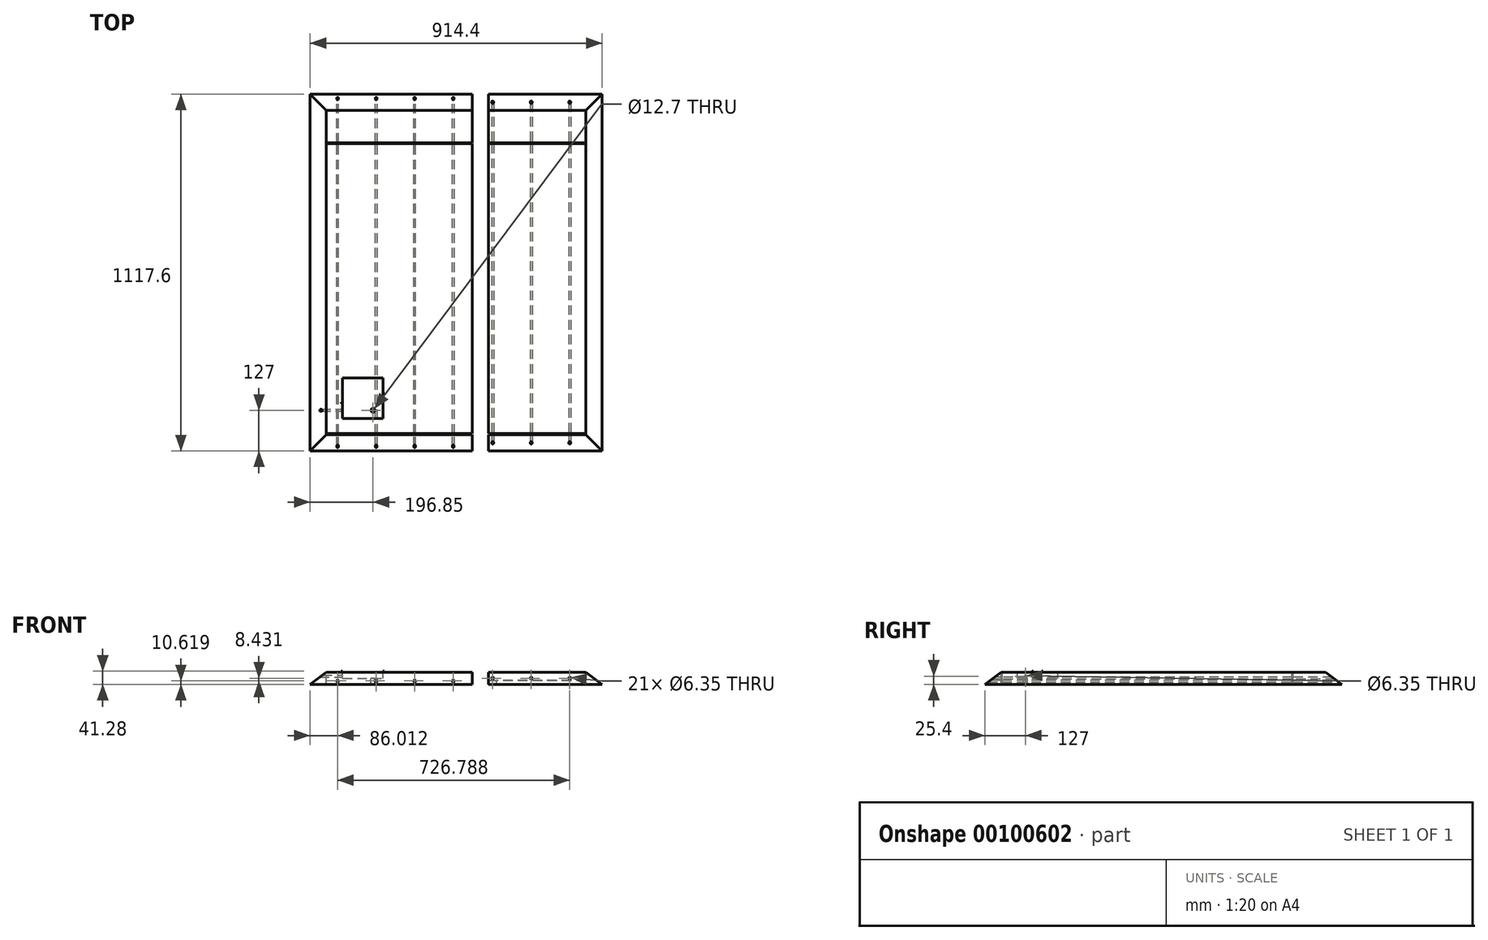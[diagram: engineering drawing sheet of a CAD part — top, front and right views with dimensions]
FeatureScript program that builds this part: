
annotation { "Feature Type Name" : "Feature", "Feature Type Description" : "" }
export const myFeature = defineFeature(function(context is Context, id is Id, definition is map)
    precondition{}
    {
        {
            var Q0;
            Q0=qCreatedBy(makeId("Top.planeOp"),FACE);
            var sketch = newSketch(context, id + "F0", { "sketchPlane" : qUnion([Q0])});
            skLineSegment(sketch, "E0.bottom", {"start": v(-406.4, 558.8) * mm, "end": v(50.8, 558.8) * mm});
            skLineSegment(sketch, "E0.top", {"start": v(-406.4, -558.8) * mm, "end": v(50.8, -558.8) * mm});
            skLineSegment(sketch, "E0.left", {"start": v(-406.4, 558.8) * mm, "end": v(-406.4, -558.8) * mm});
            skLineSegment(sketch, "E0.right", {"start": v(406.4, 558.8) * mm, "end": v(406.4, -558.8) * mm});
            skPoint(sketch, "E1", {"position": v(0, 558.8) * mm});
            skPoint(sketch, "E2.positionSnap0", {"position": v(406.4, 0) * mm});
            skLineSegment(sketch, "E3", {"start": v(101.6, 558.8) * mm, "end": v(101.6, -558.8) * mm});
            skLineSegment(sketch, "E4", {"start": v(50.8, 558.8) * mm, "end": v(50.8, -558.8) * mm});
            skLineSegment(sketch, "E5.trimOffspring", {"start": v(101.6, 558.8) * mm, "end": v(406.4, 558.8) * mm});
            skLineSegment(sketch, "E6.trimOffspring", {"start": v(101.6, -558.8) * mm, "end": v(406.4, -558.8) * mm});
            skSolve(sketch);
        }
        {
            var Q0;
            Q0=makeQuery(id+"F0.imprint","IMPRINT",FACE,{"disambiguationData":[TD([[makeQuery(id+"F0.imprint","IMPRINT",EDGE,{"derivedFrom":sQuery(id+"F0.wireOp",EDGE,"E0.bottom")}),-1.0]])]});
            extrude(context, id + "F1", {"entities" : qUnion([Q0]), "depth" : 38.1 * mm});
        }
        {
            var Q0;
            Q0=makeQuery(id+"F1.opExtrude","CAP_EDGE",EDGE,{"disambiguationData":[OSD([sQuery(id+"F0.wireOp",EDGE,"E0.top")])],"isStart":false});
            var Q1;
            Q1=makeQuery(id+"F1.opExtrude","CAP_EDGE",EDGE,{"disambiguationData":[OSD([sQuery(id+"F0.wireOp",EDGE,"E0.left")])],"isStart":false});
            var Q2;
            Q2=makeQuery(id+"F1.opExtrude","CAP_EDGE",EDGE,{"disambiguationData":[OSD([sQuery(id+"F0.wireOp",EDGE,"E0.bottom")])],"isStart":false});
            chamfer(context, id + "F2", {"entities" : qUnion([Q0, Q1, Q2]), "width" : 38.1 * mm, "tangentPropagation" : true});
        }
        {
            var Q0;
            Q0=qCreatedBy(makeId("Front.planeOp"),FACE);
            var sketch = newSketch(context, id + "F3", { "sketchPlane" : qUnion([Q0])});
            skLineSegment(sketch, "E7.bottom", {"start": v(139.7, 0) * mm, "end": v(88.9, 0) * mm});
            skLineSegment(sketch, "E7.top", {"start": v(139.7, 50.8) * mm, "end": v(88.9, 50.8) * mm});
            skLineSegment(sketch, "E7.left", {"start": v(139.7, 0) * mm, "end": v(139.7, 50.8) * mm});
            skLineSegment(sketch, "E7.right", {"start": v(88.9, 0) * mm, "end": v(88.9, 50.8) * mm});
            skPoint(sketch, "E8", {"position": v(114.3, 0) * mm});
            skSolve(sketch);
        }
        {
            var Q0;
            Q0=makeQuery(id+"F3.imprint","IMPRINT",FACE,{"disambiguationData":[TD([[makeQuery(id+"F3.imprint","IMPRINT",EDGE,{"derivedFrom":sQuery(id+"F3.wireOp",EDGE,"E7.bottom")}),-1.0]])]});
            extrude(context, id + "F4", {"entities" : qUnion([Q0]), "operationType" : NewBodyOperationType.REMOVE, "oppositeDirection" : true, "depth" : 406.4 * mm, "hasSecondDirection" : true, "secondDirectionOppositeDirection" : false, "secondDirectionDepth" : 406.4 * mm});
        }
        {
            var Q0;
            Q0=makeQuery(id+"F1.opExtrude","CAP_FACE",FACE,{"disambiguationData":[OSD([sQuery(id+"F0.wireOp",EDGE,"E0.bottom"),sQuery(id+"F0.wireOp",EDGE,"E0.top"),sQuery(id+"F0.wireOp",EDGE,"E0.left"),sQuery(id+"F0.wireOp",EDGE,"E0.right")])],"isStart":false});
            var sketch = newSketch(context, id + "F5", { "sketchPlane" : qUnion([Q0])});
            skLineSegment(sketch, "E9.bottom", {"start": v(-165.1, -520.7) * mm, "end": v(-368.3, -520.7) * mm});
            skLineSegment(sketch, "E9.top", {"start": v(-165.1, -368.3) * mm, "end": v(-368.3, -368.3) * mm});
            skLineSegment(sketch, "E9.left", {"start": v(-165.1, -520.7) * mm, "end": v(-165.1, -368.3) * mm});
            skLineSegment(sketch, "E9.right", {"start": v(-368.3, -520.7) * mm, "end": v(-368.3, -368.3) * mm});
            skSolve(sketch);
        }
        {
            var Q0;
            Q0=makeQuery(id+"F5.imprint","IMPRINT",FACE,{"disambiguationData":[TD([[makeQuery(id+"F5.imprint","IMPRINT",EDGE,{"derivedFrom":sQuery(id+"F5.wireOp",EDGE,"E9.bottom")}),-1.0]])]});
            var Q1;
            Q1=makeQuery(id+"F5.imprint","IMPRINT",FACE,{"disambiguationData":[TD([[makeQuery(id+"F5.imprint","IMPRINT",EDGE,{"derivedFrom":sQuery(id+"F5.wireOp",EDGE,"E9.bottom")}),1.0]])]});
            extrude(context, id + "F6", {"entities" : qUnion([Q0, Q1]), "operationType" : NewBodyOperationType.REMOVE, "oppositeDirection" : true, "depth" : 25.4 * mm});
        }
        {
            var Q0;
            Q0=makeQuery(id+"F1.opExtrude","SWEPT_BODY",BODY,{"disambiguationData":[OSD([sQuery(id+"F0.wireOp",EDGE,"E0.bottom"),sQuery(id+"F0.wireOp",EDGE,"E0.top"),sQuery(id+"F0.wireOp",EDGE,"E0.left"),sQuery(id+"F0.wireOp",EDGE,"E0.right")])]});
            deleteBodies(context, id + "F7", {"entities" : qUnion([Q0])});
        }
        {
            var Q0;
            Q0 = qSketchRegion(id + "F0", true);
            extrude(context, id + "F8", {"entities" : qUnion([Q0]), "depth" : 38.1 * mm});
        }
        {
            var Q0;
            Q0=makeQuery(id+"F8.opExtrude","SWEPT_FACE",FACE,{"disambiguationData":[OSD([sQuery(id+"F0.wireOp",EDGE,"E6.trimOffspring")])]});
            var sketch = newSketch(context, id + "F9", { "sketchPlane" : qUnion([Q0])});
            skLineSegment(sketch, "E10", {"start": v(406.4, 38.1) * mm, "end": v(457.2, 0) * mm});
            skLineSegment(sketch, "E11", {"start": v(457.2, 0) * mm, "end": v(406.4, 0) * mm});
            skLineSegment(sketch, "E12", {"start": v(406.4, 0) * mm, "end": v(101.6, 0) * mm});
            skLineSegment(sketch, "E13", {"start": v(101.6, 0) * mm, "end": v(101.6, 38.1) * mm});
            skLineSegment(sketch, "E14", {"start": v(101.6, 38.1) * mm, "end": v(406.4, 38.1) * mm});
            skSolve(sketch);
        }
        {
            var Q0;
            Q0=makeQuery(id+"F9.imprint","IMPRINT",FACE,{"disambiguationData":[TD([[makeQuery(id+"F9.imprint","IMPRINT",EDGE,{"derivedFrom":sQuery(id+"F9.wireOp",EDGE,"E10")}),-1.0]])]});
            var Q1;
            Q1=makeQuery(id+"F8.opExtrude","SWEPT_FACE",FACE,{"disambiguationData":[OSD([sQuery(id+"F0.wireOp",EDGE,"E5.trimOffspring")])]});
            extrude(context, id + "F10", {"entities" : qUnion([Q0]), "operationType" : NewBodyOperationType.ADD, "endBound" : BoundingType.UP_TO_SURFACE, "oppositeDirection" : true, "endBoundEntityFace" : qUnion([Q1]), "depth" : 25.4 * mm});
        }
        {
            var Q0;
            Q0 = qSketchRegion(id + "F9", true);
            var Q1;
            Q1=makeQuery(id+"F8.opExtrude","SWEPT_FACE",FACE,{"disambiguationData":[OSD([sQuery(id+"F0.wireOp",EDGE,"E5.trimOffspring")])]});
            extrude(context, id + "F11", {"entities" : qUnion([Q0]), "operationType" : NewBodyOperationType.ADD, "endBound" : BoundingType.UP_TO_SURFACE, "oppositeDirection" : true, "endBoundEntityFace" : qUnion([Q1]), "depth" : 25.4 * mm});
        }
        {
            var Q0;
            Q0=makeQuery(id+"F8.opExtrude","SWEPT_FACE",FACE,{"disambiguationData":[OSD([sQuery(id+"F0.wireOp",EDGE,"E0.top")])]});
            var sketch = newSketch(context, id + "F12", { "sketchPlane" : qUnion([Q0])});
            skLineSegment(sketch, "E15", {"start": v(-406.4, 38.1) * mm, "end": v(-457.2, 0) * mm});
            skLineSegment(sketch, "E16", {"start": v(-457.2, 0) * mm, "end": v(-406.4, 0) * mm});
            skLineSegment(sketch, "E17", {"start": v(-406.4, 0) * mm, "end": v(50.8, 0) * mm});
            skLineSegment(sketch, "E18", {"start": v(50.8, 0) * mm, "end": v(50.8, 38.1) * mm});
            skLineSegment(sketch, "E19", {"start": v(50.8, 38.1) * mm, "end": v(-406.4, 38.1) * mm});
            skSolve(sketch);
        }
        {
            var Q0;
            Q0 = qSketchRegion(id + "F12", true);
            var Q1;
            Q1=makeQuery(id+"F8.opExtrude","SWEPT_FACE",FACE,{"disambiguationData":[OSD([sQuery(id+"F0.wireOp",EDGE,"E0.bottom")])]});
            extrude(context, id + "F13", {"entities" : qUnion([Q0]), "operationType" : NewBodyOperationType.ADD, "endBound" : BoundingType.UP_TO_SURFACE, "oppositeDirection" : true, "endBoundEntityFace" : qUnion([Q1]), "depth" : 25.4 * mm});
        }
        {
            var Q0;
            Q0=makeQuery(id+"F8.opExtrude","CAP_FACE",FACE,{"disambiguationData":[OSD([sQuery(id+"F0.wireOp",EDGE,"E0.bottom"),sQuery(id+"F0.wireOp",EDGE,"E0.top"),sQuery(id+"F0.wireOp",EDGE,"E0.left"),sQuery(id+"F0.wireOp",EDGE,"E4")])],"isStart":false});
            var sketch = newSketch(context, id + "F14", { "sketchPlane" : qUnion([Q0])});
            skLineSegment(sketch, "E20.bottom", {"start": v(-355.6, -457.2) * mm, "end": v(-228.6, -457.2) * mm});
            skLineSegment(sketch, "E20.top", {"start": v(-355.6, -330.2) * mm, "end": v(-228.6, -330.2) * mm});
            skLineSegment(sketch, "E20.left", {"start": v(-355.6, -457.2) * mm, "end": v(-355.6, -330.2) * mm});
            skLineSegment(sketch, "E20.right", {"start": v(-228.6, -457.2) * mm, "end": v(-228.6, -330.2) * mm});
            skSolve(sketch);
        }
        {
            var Q0;
            Q0=makeQuery(id+"F14.imprint","IMPRINT",FACE,{"disambiguationData":[TD([[makeQuery(id+"F14.imprint","IMPRINT",EDGE,{"derivedFrom":sQuery(id+"F14.wireOp",EDGE,"E20.bottom")}),1.0]])]});
            extrude(context, id + "F15", {"entities" : qUnion([Q0]), "operationType" : NewBodyOperationType.REMOVE, "oppositeDirection" : true, "depth" : 19.05 * mm});
        }
        {
            var Q0;
            Q0=makeQuery(id+"F15.boolean.opBoolean","COPY",FACE,{"derivedFrom":makeQuery(id+"F15.opExtrude","CAP_FACE",FACE,{"disambiguationData":[OSD([sQuery(id+"F14.wireOp",EDGE,"E20.bottom"),sQuery(id+"F14.wireOp",EDGE,"E20.top"),sQuery(id+"F14.wireOp",EDGE,"E20.left"),sQuery(id+"F14.wireOp",EDGE,"E20.right")])],"isStart":false})});
            var sketch = newSketch(context, id + "F16", { "sketchPlane" : qUnion([Q0])});
            skCircle(sketch, "E21", {"center": v(-260.35, -431.8) * mm, "radius": 6.35 * mm});
            skSolve(sketch);
        }
        {
            var Q0;
            Q0 = qSketchRegion(id + "F16", true);
            extrude(context, id + "F17", {"entities" : qUnion([Q0]), "operationType" : NewBodyOperationType.REMOVE, "oppositeDirection" : true, "depth" : 25.4 * mm});
        }
        {
            var Q0;
            Q0=makeQuery(id+"F15.boolean.opBoolean","COPY",FACE,{"derivedFrom":makeQuery(id+"F15.opExtrude","SWEPT_FACE",FACE,{"disambiguationData":[OSD([sQuery(id+"F14.wireOp",EDGE,"E20.left")])]})});
            var sketch = newSketch(context, id + "F18", { "sketchPlane" : qUnion([Q0])});
            skCircle(sketch, "E22", {"center": v(-431.8, 25.4) * mm, "radius": 3.18 * mm});
            skSolve(sketch);
        }
        {
            var Q0;
            Q0=makeQuery(id+"F18.imprint","IMPRINT",FACE,{"disambiguationData":[TD([[makeQuery(id+"F18.imprint","IMPRINT",EDGE,{"derivedFrom":sQuery(id+"F18.wireOp",EDGE,"E22")}),1.0]])]});
            extrude(context, id + "F19", {"entities" : qUnion([Q0]), "operationType" : NewBodyOperationType.REMOVE, "endBound" : BoundingType.THROUGH_ALL, "oppositeDirection" : true, "depth" : 25.4 * mm});
        }
        {
            var Q0;
            Q0=makeQuery(id+"F8.opExtrude","CAP_FACE",FACE,{"disambiguationData":[OSD([sQuery(id+"F0.wireOp",EDGE,"E0.bottom"),sQuery(id+"F0.wireOp",EDGE,"E0.top"),sQuery(id+"F0.wireOp",EDGE,"E0.left"),sQuery(id+"F0.wireOp",EDGE,"E4")])],"isStart":false});
            var sketch = newSketch(context, id + "F20", { "sketchPlane" : qUnion([Q0])});
            skLineSegment(sketch, "E23.bottom", {"start": v(-361.95, -463.55) * mm, "end": v(-222.25, -463.55) * mm});
            skLineSegment(sketch, "E23.top", {"start": v(-361.95, -323.85) * mm, "end": v(-222.25, -323.85) * mm});
            skLineSegment(sketch, "E23.left", {"start": v(-361.95, -463.55) * mm, "end": v(-361.95, -323.85) * mm});
            skLineSegment(sketch, "E23.right", {"start": v(-222.25, -463.55) * mm, "end": v(-222.25, -323.85) * mm});
            skSolve(sketch);
        }
        {
            var Q0;
            Q0=makeQuery(id+"F20.imprint","IMPRINT",FACE,{"disambiguationData":[TD([[makeQuery(id+"F20.imprint","IMPRINT",EDGE,{"derivedFrom":makeQuery(id+"F15.boolean.opBoolean","COPY",EDGE,{"derivedFrom":makeQuery(id+"F15.opExtrude","CAP_EDGE",EDGE,{"disambiguationData":[OSD([sQuery(id+"F14.wireOp",EDGE,"E20.bottom")])],"isStart":true})})}),1.0]])]});
            var Q1;
            Q1=makeQuery(id+"F20.imprint","IMPRINT",FACE,{"disambiguationData":[TD([[makeQuery(id+"F20.imprint","IMPRINT",EDGE,{"derivedFrom":sQuery(id+"F20.wireOp",EDGE,"E23.bottom")}),1.0]])]});
            extrude(context, id + "F21", {"entities" : qUnion([Q0, Q1]), "depth" : 3.17 * mm});
        }
        {
            var Q0;
            Q0=makeQuery(id+"F21.opExtrude","CAP_FACE",FACE,{"disambiguationData":[OSD([sQuery(id+"F20.wireOp",EDGE,"E23.bottom"),sQuery(id+"F20.wireOp",EDGE,"E23.top"),sQuery(id+"F20.wireOp",EDGE,"E23.left"),sQuery(id+"F20.wireOp",EDGE,"E23.right")])],"isStart":false});
            var sketch = newSketch(context, id + "F22", { "sketchPlane" : qUnion([Q0])});
            skCircle(sketch, "E24", {"center": v(-357.51, -378.81) * mm, "radius": 1.65 * mm});
            skLineSegment(sketch, "E25", {"start": v(-361.95, -393.7) * mm, "end": v(-222.25, -393.7) * mm, "construction": true});
            skLineSegment(sketch, "E26", {"start": v(-292.1, -323.85) * mm, "end": v(-292.1, -463.55) * mm, "construction": true});
            skLineSegment(sketch, "E27.MirrorCS", {"start": v(-222.25, -393.7) * mm, "end": v(-361.95, -393.7) * mm, "construction": true});
            skCircle(sketch, "E28.MirrorC", {"center": v(-226.69, -378.81) * mm, "radius": 1.65 * mm});
            skCircle(sketch, "E29.MirrorC", {"center": v(-226.69, -408.59) * mm, "radius": 1.65 * mm});
            skCircle(sketch, "E30.MirrorC", {"center": v(-357.51, -408.59) * mm, "radius": 1.65 * mm});
            skSolve(sketch);
        }
        {
            var Q0;
            Q0=makeQuery(id+"F22.imprint","IMPRINT",FACE,{"disambiguationData":[TD([[makeQuery(id+"F22.imprint","IMPRINT",EDGE,{"derivedFrom":sQuery(id+"F22.wireOp",EDGE,"E30.MirrorC")}),-1.0]])]});
            var Q1;
            Q1=makeQuery(id+"F22.imprint","IMPRINT",FACE,{"disambiguationData":[TD([[makeQuery(id+"F22.imprint","IMPRINT",EDGE,{"derivedFrom":sQuery(id+"F22.wireOp",EDGE,"E29.MirrorC")}),1.0]])]});
            var Q2;
            Q2=makeQuery(id+"F22.imprint","IMPRINT",FACE,{"disambiguationData":[TD([[makeQuery(id+"F22.imprint","IMPRINT",EDGE,{"derivedFrom":sQuery(id+"F22.wireOp",EDGE,"E28.MirrorC")}),-1.0]])]});
            var Q3;
            Q3=makeQuery(id+"F22.imprint","IMPRINT",FACE,{"disambiguationData":[TD([[makeQuery(id+"F22.imprint","IMPRINT",EDGE,{"derivedFrom":sQuery(id+"F22.wireOp",EDGE,"E24")}),1.0]])]});
            extrude(context, id + "F23", {"entities" : qUnion([Q0, Q1, Q2, Q3]), "operationType" : NewBodyOperationType.REMOVE, "endBound" : BoundingType.UP_TO_NEXT, "oppositeDirection" : true, "depth" : 25.4 * mm});
        }
        {
            var Q0;
            Q0=makeQuery(id+"F13.boolean.opBoolean","MERGE",FACE,{"derivedFrom":[makeQuery(id+"F8.opExtrude","SWEPT_FACE",FACE,{"disambiguationData":[OSD([sQuery(id+"F0.wireOp",EDGE,"E0.top")])]}),makeQuery(id+"F13.opExtrude","CAP_FACE",FACE,{"disambiguationData":[OSD([sQuery(id+"F12.wireOp",EDGE,"E15"),sQuery(id+"F12.wireOp",EDGE,"E16"),sQuery(id+"F12.wireOp",EDGE,"E17"),sQuery(id+"F12.wireOp",EDGE,"E18"),sQuery(id+"F12.wireOp",EDGE,"E19")])],"isStart":true})]});
            var sketch = newSketch(context, id + "F24", { "sketchPlane" : qUnion([Q0])});
            skLineSegment(sketch, "E31", {"start": v(-457.2, 0) * mm, "end": v(-406.4, 38.1) * mm});
            skLineSegment(sketch, "E32.0.0", {"start": v(101.6, 0) * mm, "end": v(457.2, 0) * mm});
            skLineSegment(sketch, "E32.0.1", {"start": v(457.2, 0) * mm, "end": v(406.4, 38.1) * mm});
            skLineSegment(sketch, "E32.0.2", {"start": v(406.4, 38.1) * mm, "end": v(101.6, 38.1) * mm});
            skLineSegment(sketch, "E33", {"start": v(50.8, 38.1) * mm, "end": v(50.8, 0) * mm});
            skLineSegment(sketch, "E34", {"start": v(-406.4, 38.1) * mm, "end": v(50.8, 38.1) * mm});
            skLineSegment(sketch, "E35", {"start": v(-457.2, 0) * mm, "end": v(50.8, 0) * mm});
            skSolve(sketch);
        }
        {
            var Q0;
            Q0=makeQuery(id+"F8.opExtrude","CAP_EDGE",EDGE,{"disambiguationData":[OSD([sQuery(id+"F0.wireOp",EDGE,"E0.bottom")])],"isStart":false});
            var Q1;
            Q1=makeQuery(id+"F8.opExtrude","CAP_EDGE",EDGE,{"disambiguationData":[OSD([sQuery(id+"F0.wireOp",EDGE,"E5.trimOffspring")])],"isStart":false});
            var Q2;
            Q2=makeQuery(id+"F8.opExtrude","CAP_EDGE",EDGE,{"disambiguationData":[OSD([sQuery(id+"F0.wireOp",EDGE,"E0.top")])],"isStart":false});
            var Q3;
            Q3=makeQuery(id+"F8.opExtrude","CAP_EDGE",EDGE,{"disambiguationData":[OSD([sQuery(id+"F0.wireOp",EDGE,"E6.trimOffspring")])],"isStart":false});
            chamfer(context, id + "F25", {"entities" : qUnion([Q0, Q1, Q2, Q3]), "chamferType" : ChamferType.TWO_OFFSETS, "width1" : 38.1 * mm, "oppositeDirection" : false, "width2" : 50.8 * mm});
        }
        {
            var Q0;
            Q0=makeQuery(id+"F8.opExtrude","CAP_FACE",FACE,{"disambiguationData":[OSD([sQuery(id+"F0.wireOp",EDGE,"E0.bottom"),sQuery(id+"F0.wireOp",EDGE,"E0.top"),sQuery(id+"F0.wireOp",EDGE,"E0.left"),sQuery(id+"F0.wireOp",EDGE,"E4")])],"isStart":false});
            var sketch = newSketch(context, id + "F26", { "sketchPlane" : qUnion([Q0])});
            skLineSegment(sketch, "E36.bottom", {"start": v(-406.4, -504.83) * mm, "end": v(127, -504.83) * mm});
            skLineSegment(sketch, "E36.top", {"start": v(-406.4, -508) * mm, "end": v(127, -508) * mm});
            skLineSegment(sketch, "E36.left", {"start": v(-406.4, -504.83) * mm, "end": v(-406.4, -508) * mm});
            skLineSegment(sketch, "E36.right", {"start": v(127, -504.83) * mm, "end": v(127, -508) * mm});
            skLineSegment(sketch, "E37.bottom", {"start": v(-406.4, 406.4) * mm, "end": v(50.8, 406.4) * mm});
            skLineSegment(sketch, "E37.top", {"start": v(-406.4, 403.23) * mm, "end": v(50.8, 403.23) * mm});
            skLineSegment(sketch, "E37.left", {"start": v(-406.4, 406.4) * mm, "end": v(-406.4, 403.23) * mm});
            skLineSegment(sketch, "E37.right", {"start": v(50.8, 406.4) * mm, "end": v(50.8, 403.23) * mm});
            skSolve(sketch);
        }
        {
            var Q0;
            Q0 = qSketchRegion(id + "F26", true);
            extrude(context, id + "F27", {"entities" : qUnion([Q0]), "operationType" : NewBodyOperationType.REMOVE, "endBound" : BoundingType.THROUGH_ALL, "oppositeDirection" : true, "depth" : 25.4 * mm});
        }
        {
            var Q0;
            Q0 = qSketchRegion(id + "F26", true);
            extrude(context, id + "F28", {"entities" : qUnion([Q0]), "operationType" : NewBodyOperationType.REMOVE, "endBound" : BoundingType.THROUGH_ALL, "oppositeDirection" : true, "depth" : 25.4 * mm});
        }
        {
            var Q0;
            Q0=makeQuery(id+"F8.opExtrude","CAP_FACE",FACE,{"disambiguationData":[OSD([sQuery(id+"F0.wireOp",EDGE,"E0.right"),sQuery(id+"F0.wireOp",EDGE,"E3"),sQuery(id+"F0.wireOp",EDGE,"E5.trimOffspring"),sQuery(id+"F0.wireOp",EDGE,"E6.trimOffspring")])],"isStart":false});
            var sketch = newSketch(context, id + "F29", { "sketchPlane" : qUnion([Q0])});
            skLineSegment(sketch, "E38.bottom", {"start": v(406.4, -508) * mm, "end": v(101.6, -508) * mm});
            skLineSegment(sketch, "E38.top", {"start": v(406.4, -504.83) * mm, "end": v(101.6, -504.83) * mm});
            skLineSegment(sketch, "E38.left", {"start": v(406.4, -508) * mm, "end": v(406.4, -504.83) * mm});
            skLineSegment(sketch, "E38.right", {"start": v(101.6, -508) * mm, "end": v(101.6, -504.83) * mm});
            skLineSegment(sketch, "E39.bottom", {"start": v(101.6, 406.4) * mm, "end": v(406.4, 406.4) * mm});
            skLineSegment(sketch, "E39.top", {"start": v(101.6, 403.22) * mm, "end": v(406.4, 403.22) * mm});
            skLineSegment(sketch, "E39.left", {"start": v(101.6, 406.4) * mm, "end": v(101.6, 403.22) * mm});
            skLineSegment(sketch, "E39.right", {"start": v(406.4, 406.4) * mm, "end": v(406.4, 403.22) * mm});
            skSolve(sketch);
        }
        {
            var Q0;
            Q0 = qSketchRegion(id + "F29", true);
            extrude(context, id + "F30", {"entities" : qUnion([Q0]), "operationType" : NewBodyOperationType.REMOVE, "oppositeDirection" : true, "depth" : 25.4 * mm});
        }
        {
            var Q0;
            Q0=qCreatedBy(makeId("Front.planeOp"),FACE);
            var sketch = newSketch(context, id + "F31", { "sketchPlane" : qUnion([Q0])});
            skCircle(sketch, "E40", {"center": v(355.6, 19.05) * mm, "radius": 3.18 * mm});
            skCircle(sketch, "E41.1.0.0", {"center": v(234.95, 19.05) * mm, "radius": 3.18 * mm});
            skCircle(sketch, "E41.2.0.0", {"center": v(114.3, 19.05) * mm, "radius": 3.18 * mm});
            skLineSegment(sketch, "E41.direction1", {"start": v(355.6, 19.05) * mm, "end": v(234.95, 19.05) * mm, "construction": true});
            skSolve(sketch);
        }
        {
            var Q0;
            Q0 = qSketchRegion(id + "F31", true);
            extrude(context, id + "F32", {"entities" : qUnion([Q0]), "operationType" : NewBodyOperationType.REMOVE, "endBound" : BoundingType.THROUGH_ALL, "oppositeDirection" : true, "depth" : 25.4 * mm, "hasSecondDirection" : true, "secondDirectionBound" : SecondDirectionBoundingType.THROUGH_ALL, "secondDirectionOppositeDirection" : false, "secondDirectionDepth" : 25.4 * mm});
        }
        {
            var Q0;
            Q0=qCreatedBy(makeId("Front.planeOp"),FACE);
            var sketch = newSketch(context, id + "F33", { "sketchPlane" : qUnion([Q0])});
            skCircle(sketch, "E42", {"center": v(-9.24, 10.62) * mm, "radius": 3.18 * mm});
            skCircle(sketch, "E43.1.0.0", {"center": v(-129.89, 10.62) * mm, "radius": 3.18 * mm});
            skCircle(sketch, "E43.2.0.0", {"center": v(-250.54, 10.62) * mm, "radius": 3.18 * mm});
            skCircle(sketch, "E43.3.0.0", {"center": v(-371.19, 10.62) * mm, "radius": 3.18 * mm});
            skLineSegment(sketch, "E43.direction1", {"start": v(-9.24, 10.62) * mm, "end": v(-129.89, 10.62) * mm, "construction": true});
            skSolve(sketch);
        }
        {
            var Q0;
            Q0 = qSketchRegion(id + "F33", true);
            extrude(context, id + "F34", {"entities" : qUnion([Q0]), "operationType" : NewBodyOperationType.REMOVE, "endBound" : BoundingType.THROUGH_ALL, "depth" : 25.4 * mm, "hasSecondDirection" : true, "secondDirectionBound" : SecondDirectionBoundingType.THROUGH_ALL, "secondDirectionOppositeDirection" : true, "secondDirectionDepth" : 25.4 * mm});
        }
    });
